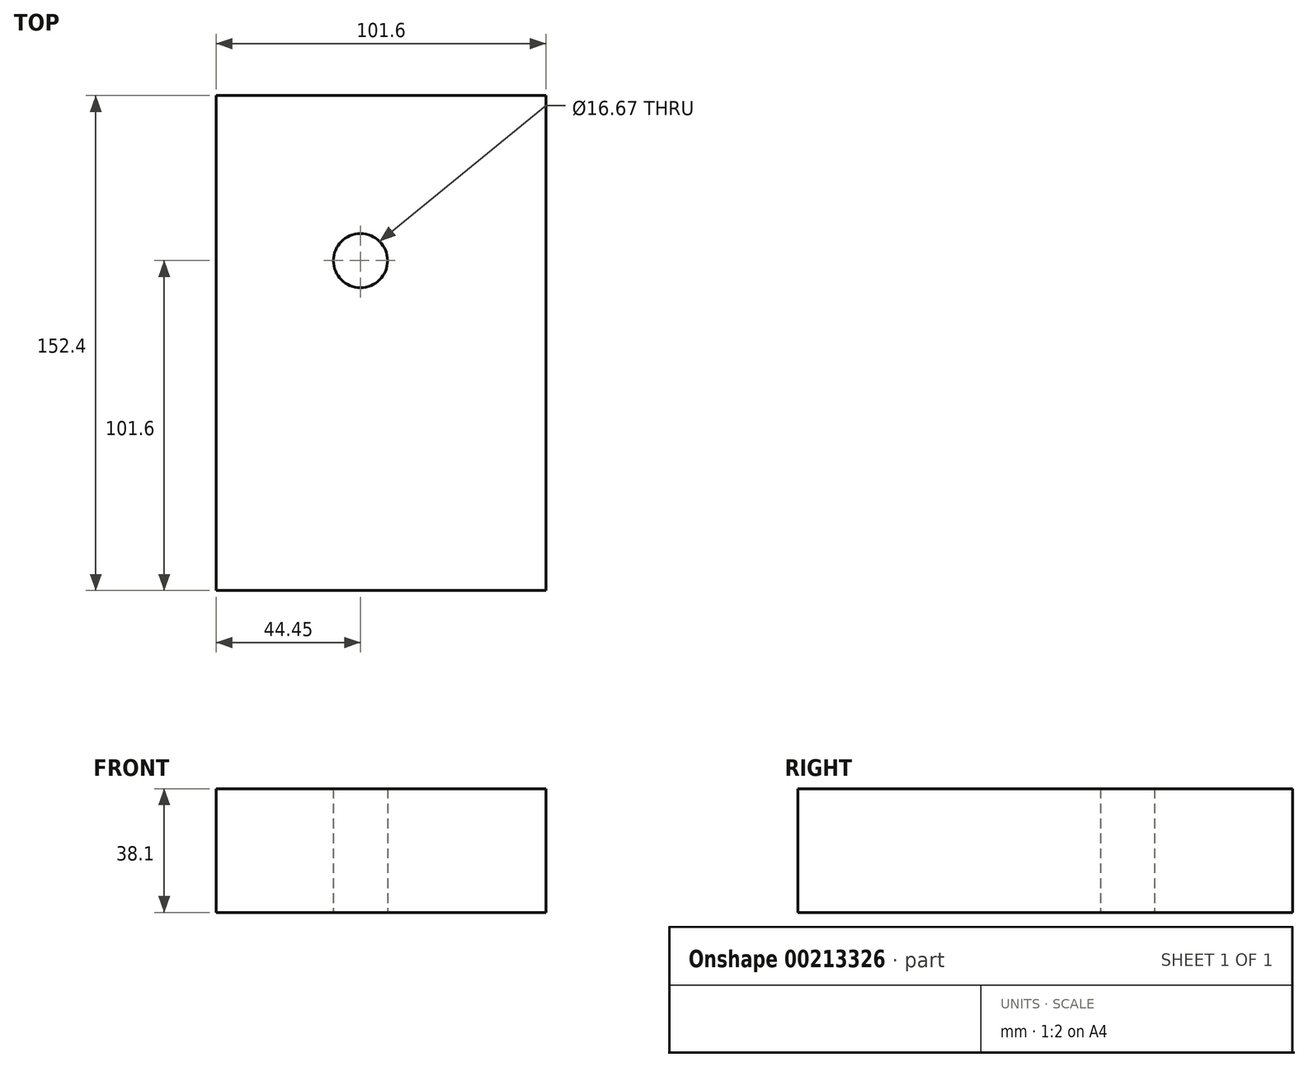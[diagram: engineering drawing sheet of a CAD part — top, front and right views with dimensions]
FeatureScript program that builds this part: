
annotation { "Feature Type Name" : "Feature", "Feature Type Description" : "" }
export const myFeature = defineFeature(function(context is Context, id is Id, definition is map)
    precondition{}
    {
        {
            var Q0;
            Q0=qCreatedBy(makeId("Top.planeOp"),FACE);
            var sketch = newSketch(context, id + "F0", { "sketchPlane" : qUnion([Q0])});
            skLineSegment(sketch, "E0.bottom", {"start": v(-50.8, -76.2) * mm, "end": v(50.8, -76.2) * mm});
            skLineSegment(sketch, "E0.top", {"start": v(-50.8, 76.2) * mm, "end": v(50.8, 76.2) * mm});
            skLineSegment(sketch, "E0.left", {"start": v(-50.8, -76.2) * mm, "end": v(-50.8, 76.2) * mm});
            skLineSegment(sketch, "E0.right", {"start": v(50.8, -76.2) * mm, "end": v(50.8, 76.2) * mm});
            skPoint(sketch, "E0.middle", {"position": v(0, 0) * mm});
            skPoint(sketch, "E1", {"position": v(-6.35, 25.4) * mm});
            skCircle(sketch, "E2", {"center": v(-6.35, 25.4) * mm, "radius": 8.33 * mm});
            skSolve(sketch);
        }
        {
            var Q0;
            Q0=makeQuery(id+"F0.imprint","IMPRINT",FACE,{"disambiguationData":[TD([[makeQuery(id+"F0.imprint","IMPRINT",EDGE,{"derivedFrom":sQuery(id+"F0.wireOp",EDGE,"E0.bottom")}),1.0]])]});
            extrude(context, id + "F1", {"entities" : qUnion([Q0]), "depth" : 38.1 * mm});
        }
    });
